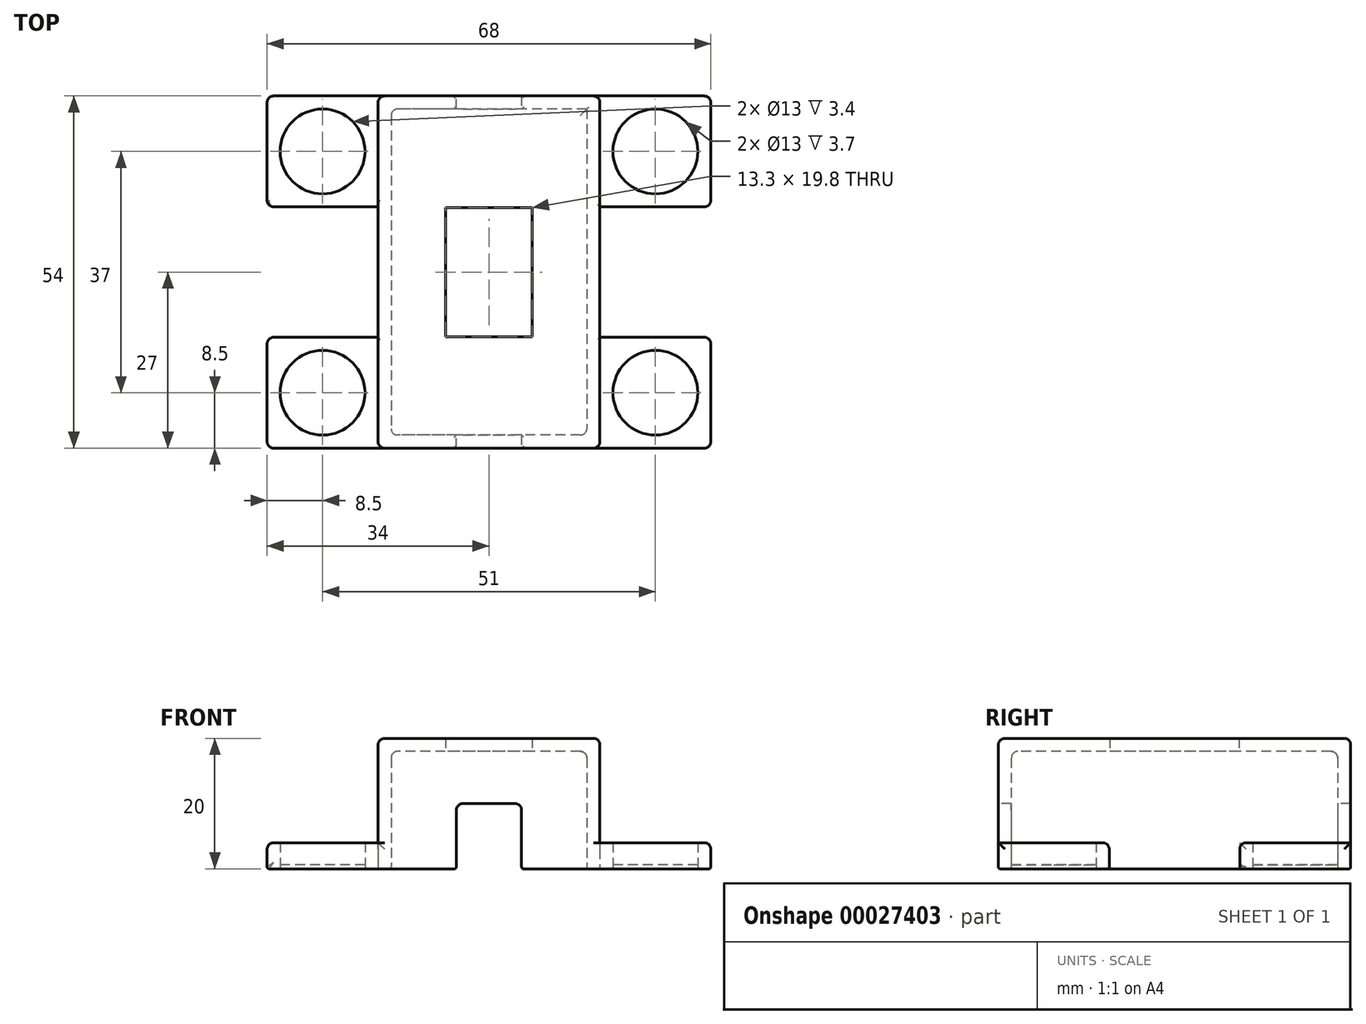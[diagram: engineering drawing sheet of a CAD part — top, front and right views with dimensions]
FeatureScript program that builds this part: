
annotation { "Feature Type Name" : "Feature", "Feature Type Description" : "" }
export const myFeature = defineFeature(function(context is Context, id is Id, definition is map)
    precondition{}
    {
        {
            assignVariable(context, id + "F0", {"name" : "PrintTolerance", "anyValue" : .3});
        }
        {
            assignVariable(context, id + "F1", {"name" : "Height", "anyValue" : 20});
        }
        {
            assignVariable(context, id + "F2", {"name" : "WallThickness", "anyValue" : 2});
        }
        {
            var Q0;
            Q0=qCreatedBy(makeId("Top.planeOp"),FACE);
            var sketch = newSketch(context, id + "F3", { "sketchPlane" : qUnion([Q0])});
            skLineSegment(sketch, "E0.rect.bottom", {"start": v(17, 27) * mm, "end": v(-17, 27) * mm});
            skLineSegment(sketch, "E0.rect.top", {"start": v(17, -27) * mm, "end": v(-17, -27) * mm});
            skLineSegment(sketch, "E0.rect.left", {"start": v(17, 27) * mm, "end": v(17, -27) * mm});
            skLineSegment(sketch, "E0.rect.right", {"start": v(-17, 27) * mm, "end": v(-17, -27) * mm});
            skPoint(sketch, "E0.rect.middle", {"position": v(0, 0) * mm});
            skLineSegment(sketch, "E1", {"start": v(0, -27) * mm, "end": v(0, 27) * mm, "construction": true});
            skLineSegment(sketch, "E2.0", {"start": v(-15, 25) * mm, "end": v(-15, -25) * mm});
            skLineSegment(sketch, "E2.1", {"start": v(15, 25) * mm, "end": v(-15, 25) * mm});
            skLineSegment(sketch, "E2.2", {"start": v(15, 25) * mm, "end": v(15, -25) * mm});
            skLineSegment(sketch, "E2.3", {"start": v(15, -25) * mm, "end": v(-15, -25) * mm});
            skCircle(sketch, "E3", {"center": v(-25.5, 18.5) * mm, "radius": 6.5 * mm});
            skLineSegment(sketch, "E4", {"start": v(-17, 27) * mm, "end": v(-34, 27) * mm});
            skLineSegment(sketch, "E5", {"start": v(-34, 27) * mm, "end": v(-34, 10) * mm});
            skLineSegment(sketch, "E6", {"start": v(-34, 10) * mm, "end": v(-17, 10) * mm});
            skLineSegment(sketch, "E7.MirrorCS", {"start": v(34, 10) * mm, "end": v(17, 10) * mm});
            skCircle(sketch, "E8.MirrorC", {"center": v(25.5, 18.5) * mm, "radius": 6.5 * mm});
            skLineSegment(sketch, "E9.MirrorCS", {"start": v(34, 27) * mm, "end": v(34, 10) * mm});
            skLineSegment(sketch, "E10.MirrorCS", {"start": v(17, 27) * mm, "end": v(34, 27) * mm});
            skLineSegment(sketch, "E11", {"start": v(-17, 0) * mm, "end": v(17, 0) * mm, "construction": true});
            skCircle(sketch, "E12.MirrorC", {"center": v(25.5, -18.5) * mm, "radius": 6.5 * mm});
            skLineSegment(sketch, "E13.MirrorCS", {"start": v(34, -27) * mm, "end": v(34, -10) * mm});
            skLineSegment(sketch, "E14.MirrorCS", {"start": v(17, -27) * mm, "end": v(34, -27) * mm});
            skLineSegment(sketch, "E15.MirrorCS", {"start": v(34, -10) * mm, "end": v(17, -10) * mm});
            skLineSegment(sketch, "E16.MirrorCS", {"start": v(-34, -10) * mm, "end": v(-17, -10) * mm});
            skLineSegment(sketch, "E17.MirrorCS", {"start": v(-34, -27) * mm, "end": v(-34, -10) * mm});
            skLineSegment(sketch, "E18.MirrorCS", {"start": v(-17, -27) * mm, "end": v(-34, -27) * mm});
            skCircle(sketch, "E19.MirrorC", {"center": v(-25.5, -18.5) * mm, "radius": 6.5 * mm});
            skLineSegment(sketch, "E20.bottom", {"start": v(6.65, 9.9) * mm, "end": v(-6.65, 9.9) * mm});
            skLineSegment(sketch, "E20.top", {"start": v(6.65, -9.9) * mm, "end": v(-6.65, -9.9) * mm});
            skLineSegment(sketch, "E20.left", {"start": v(6.65, 9.9) * mm, "end": v(6.65, -9.9) * mm});
            skLineSegment(sketch, "E20.right", {"start": v(-6.65, 9.9) * mm, "end": v(-6.65, -9.9) * mm});
            skSolve(sketch);
        }
        {
            var Q0;
            {var subQ4=sQuery(id+"F3.wireOp",EDGE,"E0.rect.bottom");Q0=makeQuery(id+"F3.imprint","IMPRINT",FACE,{"disambiguationData":[TD([[makeQuery(id+"F3.imprint","IMPRINT",EDGE,{"derivedFrom":subQ4}),1.0]])]});}
            var Q1;
            Q1=makeQuery(id+"F3.imprint","IMPRINT",FACE,{"disambiguationData":[TD([[makeQuery(id+"F3.imprint","IMPRINT",EDGE,{"derivedFrom":sQuery(id+"F3.wireOp",EDGE,"01951cff-519c-4d8f-8b17-a8ba54bfdcde")}),1.0]])]});
            var Q2;
            Q2=makeQuery(id+"F3.imprint","IMPRINT",FACE,{"disambiguationData":[TD([[makeQuery(id+"F3.imprint","IMPRINT",EDGE,{"derivedFrom":sQuery(id+"F3.wireOp",EDGE,"01951cff-519c-4d8f-8b17-a8ba54bfdcde")}),-1.0]])]});
            var Q3;
            Q3=makeQuery(id+"F3.imprint","IMPRINT",FACE,{"disambiguationData":[TD([[makeQuery(id+"F3.imprint","IMPRINT",EDGE,{"derivedFrom":sQuery(id+"F3.wireOp",EDGE,"E2.0")}),1.0]])]});
            extrude(context, id + "F4", {"entities" : qUnion([Q0, Q1, Q2, Q3]), "depth" : (getVariable(context, 'Height')) * mm});
        }
        {
            var Q0;
            Q0=makeQuery(id+"F3.imprint","IMPRINT",FACE,{"disambiguationData":[TD([[makeQuery(id+"F3.imprint","IMPRINT",EDGE,{"derivedFrom":sQuery(id+"F3.wireOp",EDGE,"E2.0")}),1.0]])]});
            extrude(context, id + "F5", {"entities" : qUnion([Q0]), "operationType" : NewBodyOperationType.REMOVE, "depth" : (getVariable(context, 'Height') - getVariable(context, 'WallThickness')) * mm});
        }
        {
            var Q0;
            Q0=makeQuery(id+"F3.imprint","IMPRINT",FACE,{"disambiguationData":[TD([[makeQuery(id+"F3.imprint","IMPRINT",EDGE,{"derivedFrom":sQuery(id+"F3.wireOp",EDGE,"E3")}),-1.0]])]});
            var Q1;
            {var subQ1=sQuery(id+"F3.wireOp",EDGE,"E7.MirrorCS");Q1=makeQuery(id+"F3.imprint","IMPRINT",FACE,{"disambiguationData":[TD([[makeQuery(id+"F3.imprint","IMPRINT",EDGE,{"derivedFrom":subQ1}),-1.0]])]});}
            var Q2;
            Q2=makeQuery(id+"F3.imprint","IMPRINT",FACE,{"disambiguationData":[TD([[makeQuery(id+"F3.imprint","IMPRINT",EDGE,{"derivedFrom":sQuery(id+"F3.wireOp",EDGE,"E12.MirrorC")}),-1.0]])]});
            var Q3;
            {var subQ1=sQuery(id+"F3.wireOp",EDGE,"E16.MirrorCS");Q3=makeQuery(id+"F3.imprint","IMPRINT",FACE,{"disambiguationData":[TD([[makeQuery(id+"F3.imprint","IMPRINT",EDGE,{"derivedFrom":subQ1}),-1.0]])]});}
            extrude(context, id + "F6", {"entities" : qUnion([Q0, Q1, Q2, Q3]), "operationType" : NewBodyOperationType.ADD, "depth" : 4 * mm});
        }
        {
            var Q0;
            Q0=makeQuery(id+"F3.imprint","IMPRINT",FACE,{"disambiguationData":[TD([[makeQuery(id+"F3.imprint","IMPRINT",EDGE,{"derivedFrom":sQuery(id+"F3.wireOp",EDGE,"E8.MirrorC")}),-1.0]])]});
            var Q1;
            Q1=makeQuery(id+"F3.imprint","IMPRINT",FACE,{"disambiguationData":[TD([[makeQuery(id+"F3.imprint","IMPRINT",EDGE,{"derivedFrom":sQuery(id+"F3.wireOp",EDGE,"E12.MirrorC")}),1.0]])]});
            var Q2;
            Q2=makeQuery(id+"F3.imprint","IMPRINT",FACE,{"disambiguationData":[TD([[makeQuery(id+"F3.imprint","IMPRINT",EDGE,{"derivedFrom":sQuery(id+"F3.wireOp",EDGE,"E19.MirrorC")}),-1.0]])]});
            var Q3;
            Q3=makeQuery(id+"F3.imprint","IMPRINT",FACE,{"disambiguationData":[TD([[makeQuery(id+"F3.imprint","IMPRINT",EDGE,{"derivedFrom":sQuery(id+"F3.wireOp",EDGE,"E3")}),1.0]])]});
            extrude(context, id + "F7", {"entities" : qUnion([Q0, Q1, Q2, Q3]), "operationType" : NewBodyOperationType.ADD, "depth" : .6 * mm});
        }
        {
            var Q0;
            Q0=makeQuery(id+"F6.boolean.opBoolean","MERGE",FACE,{"derivedFrom":[makeQuery(id+"F4.opExtrude","SWEPT_FACE",FACE,{"disambiguationData":[OSD([sQuery(id+"F3.wireOp",EDGE,"E0.rect.top")])]}),makeQuery(id+"F6.opExtrude","SWEPT_FACE",FACE,{"disambiguationData":[OSD([sQuery(id+"F3.wireOp",EDGE,"E14.MirrorCS")])]}),makeQuery(id+"F6.opExtrude","SWEPT_FACE",FACE,{"disambiguationData":[OSD([sQuery(id+"F3.wireOp",EDGE,"E18.MirrorCS")])]})]});
            var sketch = newSketch(context, id + "F8", { "sketchPlane" : qUnion([Q0])});
            skLineSegment(sketch, "E21", {"start": v(-5, 0) * mm, "end": v(-5, 10) * mm});
            skLineSegment(sketch, "E22", {"start": v(-5, 10) * mm, "end": v(5, 10) * mm});
            skLineSegment(sketch, "E23", {"start": v(5, 10) * mm, "end": v(5, 0) * mm});
            skLineSegment(sketch, "E24", {"start": v(-5, 0) * mm, "end": v(-5, -3) * mm});
            skLineSegment(sketch, "E25", {"start": v(-5, -3) * mm, "end": v(5, -3) * mm});
            skLineSegment(sketch, "E26", {"start": v(5, -3) * mm, "end": v(5, 0) * mm});
            skSolve(sketch);
        }
        {
            var Q0;
            {var subQ0=sQuery(id+"F8.wireOp",EDGE,"E22");Q0=makeQuery(id+"F8.imprint","IMPRINT",FACE,{"disambiguationData":[TD([[makeQuery(id+"F8.imprint","IMPRINT",EDGE,{"derivedFrom":subQ0}),-1.0]])]});}
            var Q1;
            {var subQ0=sQuery(id+"F8.wireOp",EDGE,"E24");Q1=makeQuery(id+"F8.imprint","IMPRINT",FACE,{"disambiguationData":[TD([[makeQuery(id+"F8.imprint","IMPRINT",EDGE,{"derivedFrom":subQ0}),1.0]])]});}
            extrude(context, id + "F9", {"entities" : qUnion([Q0, Q1]), "operationType" : NewBodyOperationType.REMOVE, "endBound" : BoundingType.THROUGH_ALL, "oppositeDirection" : true, "depth" : 25 * mm});
        }
        {
            var Q0;
            Q0=makeQuery(id+"F6.opExtrude","SWEPT_EDGE",EDGE,{"disambiguationData":[OSD([sQuery(id+"F3.wireOp",EDGE,"E17.MirrorCS"),sQuery(id+"F3.wireOp",EDGE,"E18.MirrorCS")])]});
            var Q1;
            Q1=makeQuery(id+"F6.opExtrude","SWEPT_EDGE",EDGE,{"disambiguationData":[OSD([sQuery(id+"F3.wireOp",EDGE,"E16.MirrorCS"),sQuery(id+"F3.wireOp",EDGE,"E17.MirrorCS")])]});
            var Q2;
            {var subQ0=sQuery(id+"F3.wireOp",EDGE,"E0.rect.right");Q2=makeQuery(id+"F6.opExtrude","CAP_EDGE",EDGE,{"disambiguationData":[OSD([subQ0]),TDD([makeQuery(id+"F3.imprint","IMPRINT",EDGE,{"disambiguationData":[TD([[makeQuery(id+"F3.imprint","INTERSECT",VERTEX,{"derivedFrom":[subQ0,sQuery(id+"F3.wireOp",EDGE,"E16.MirrorCS")]}),-1.0]])],"derivedFrom":subQ0})])],"isStart":false});}
            var Q3;
            Q3=makeQuery(id+"F6.opExtrude","SWEPT_EDGE",EDGE,{"disambiguationData":[OSD([sQuery(id+"F3.wireOp",EDGE,"E0.rect.right"),sQuery(id+"F3.wireOp",EDGE,"E16.MirrorCS")])]});
            var Q4;
            Q4=makeQuery(id+"F6.opExtrude","SWEPT_EDGE",EDGE,{"disambiguationData":[OSD([sQuery(id+"F3.wireOp",EDGE,"E0.rect.right"),sQuery(id+"F3.wireOp",EDGE,"E6")])]});
            var Q5;
            Q5=makeQuery(id+"F6.opExtrude","SWEPT_EDGE",EDGE,{"disambiguationData":[OSD([sQuery(id+"F3.wireOp",EDGE,"E5"),sQuery(id+"F3.wireOp",EDGE,"E6")])]});
            var Q6;
            Q6=makeQuery(id+"F6.opExtrude","SWEPT_EDGE",EDGE,{"disambiguationData":[OSD([sQuery(id+"F3.wireOp",EDGE,"E4"),sQuery(id+"F3.wireOp",EDGE,"E5")])]});
            var Q7;
            {var subQ0=sQuery(id+"F3.wireOp",EDGE,"E0.rect.right");Q7=makeQuery(id+"F6.opExtrude","CAP_EDGE",EDGE,{"disambiguationData":[OSD([subQ0]),TDD([makeQuery(id+"F3.imprint","IMPRINT",EDGE,{"disambiguationData":[TD([[makeQuery(id+"F3.imprint","INTERSECT",VERTEX,{"derivedFrom":[subQ0,sQuery(id+"F3.wireOp",EDGE,"E6")]}),1.0]])],"derivedFrom":subQ0})])],"isStart":false});}
            var Q8;
            Q8=makeQuery(id+"F6.opExtrude","SWEPT_EDGE",EDGE,{"disambiguationData":[OSD([sQuery(id+"F3.wireOp",EDGE,"E0.rect.left"),sQuery(id+"F3.wireOp",EDGE,"E7.MirrorCS")])]});
            var Q9;
            {var subQ0=sQuery(id+"F3.wireOp",EDGE,"E0.rect.left");Q9=makeQuery(id+"F6.opExtrude","CAP_EDGE",EDGE,{"disambiguationData":[OSD([subQ0]),TDD([makeQuery(id+"F3.imprint","IMPRINT",EDGE,{"disambiguationData":[TD([[makeQuery(id+"F3.imprint","INTERSECT",VERTEX,{"derivedFrom":[subQ0,sQuery(id+"F3.wireOp",EDGE,"E7.MirrorCS")]}),1.0]])],"derivedFrom":subQ0})])],"isStart":false});}
            var Q10;
            Q10=makeQuery(id+"F6.opExtrude","SWEPT_EDGE",EDGE,{"disambiguationData":[OSD([sQuery(id+"F3.wireOp",EDGE,"E7.MirrorCS"),sQuery(id+"F3.wireOp",EDGE,"E9.MirrorCS")])]});
            var Q11;
            Q11=makeQuery(id+"F6.opExtrude","SWEPT_EDGE",EDGE,{"disambiguationData":[OSD([sQuery(id+"F3.wireOp",EDGE,"E9.MirrorCS"),sQuery(id+"F3.wireOp",EDGE,"E10.MirrorCS")])]});
            var Q12;
            Q12=makeQuery(id+"F6.opExtrude","SWEPT_EDGE",EDGE,{"disambiguationData":[OSD([sQuery(id+"F3.wireOp",EDGE,"E13.MirrorCS"),sQuery(id+"F3.wireOp",EDGE,"E15.MirrorCS")])]});
            var Q13;
            {var subQ0=sQuery(id+"F3.wireOp",EDGE,"E0.rect.left");Q13=makeQuery(id+"F6.opExtrude","CAP_EDGE",EDGE,{"disambiguationData":[OSD([subQ0]),TDD([makeQuery(id+"F3.imprint","IMPRINT",EDGE,{"disambiguationData":[TD([[makeQuery(id+"F3.imprint","INTERSECT",VERTEX,{"derivedFrom":[subQ0,sQuery(id+"F3.wireOp",EDGE,"E15.MirrorCS")]}),-1.0]])],"derivedFrom":subQ0})])],"isStart":false});}
            var Q14;
            Q14=makeQuery(id+"F6.opExtrude","SWEPT_EDGE",EDGE,{"disambiguationData":[OSD([sQuery(id+"F3.wireOp",EDGE,"E13.MirrorCS"),sQuery(id+"F3.wireOp",EDGE,"E14.MirrorCS")])]});
            var Q15;
            Q15=makeQuery(id+"F6.opExtrude","SWEPT_EDGE",EDGE,{"disambiguationData":[OSD([sQuery(id+"F3.wireOp",EDGE,"E0.rect.left"),sQuery(id+"F3.wireOp",EDGE,"E15.MirrorCS")])]});
            var Q16;
            Q16=makeQuery(id+"F4.opExtrude","SWEPT_EDGE",EDGE,{"disambiguationData":[OSD([sQuery(id+"F3.wireOp",EDGE,"E0.rect.bottom"),sQuery(id+"F3.wireOp",EDGE,"E0.rect.left"),sQuery(id+"F3.wireOp",EDGE,"E10.MirrorCS")])]});
            var Q17;
            Q17=makeQuery(id+"F6.opExtrude","CAP_EDGE",EDGE,{"disambiguationData":[OSD([sQuery(id+"F3.wireOp",EDGE,"E9.MirrorCS")])],"isStart":false});
            var Q18;
            Q18=makeQuery(id+"F6.opExtrude","CAP_EDGE",EDGE,{"disambiguationData":[OSD([sQuery(id+"F3.wireOp",EDGE,"E7.MirrorCS")])],"isStart":false});
            var Q19;
            Q19=makeQuery(id+"F4.opExtrude","SWEPT_EDGE",EDGE,{"disambiguationData":[OSD([sQuery(id+"F3.wireOp",EDGE,"E0.rect.bottom"),sQuery(id+"F3.wireOp",EDGE,"E0.rect.right"),sQuery(id+"F3.wireOp",EDGE,"E4")])]});
            var Q20;
            Q20=makeQuery(id+"F6.opExtrude","CAP_EDGE",EDGE,{"disambiguationData":[OSD([sQuery(id+"F3.wireOp",EDGE,"E4")])],"isStart":false});
            var Q21;
            Q21=makeQuery(id+"F6.opExtrude","CAP_EDGE",EDGE,{"disambiguationData":[OSD([sQuery(id+"F3.wireOp",EDGE,"E5")])],"isStart":false});
            var Q22;
            Q22=makeQuery(id+"F6.opExtrude","CAP_EDGE",EDGE,{"disambiguationData":[OSD([sQuery(id+"F3.wireOp",EDGE,"E6")])],"isStart":true});
            var Q23;
            Q23=makeQuery(id+"F4.opExtrude","SWEPT_EDGE",EDGE,{"disambiguationData":[OSD([sQuery(id+"F3.wireOp",EDGE,"E0.rect.top"),sQuery(id+"F3.wireOp",EDGE,"E0.rect.right"),sQuery(id+"F3.wireOp",EDGE,"E18.MirrorCS")])]});
            var Q24;
            Q24=makeQuery(id+"F6.opExtrude","CAP_EDGE",EDGE,{"disambiguationData":[OSD([sQuery(id+"F3.wireOp",EDGE,"E17.MirrorCS")])],"isStart":false});
            var Q25;
            Q25=makeQuery(id+"F6.opExtrude","CAP_EDGE",EDGE,{"disambiguationData":[OSD([sQuery(id+"F3.wireOp",EDGE,"E16.MirrorCS")])],"isStart":false});
            var Q26;
            Q26=makeQuery(id+"F4.opExtrude","SWEPT_EDGE",EDGE,{"disambiguationData":[OSD([sQuery(id+"F3.wireOp",EDGE,"E0.rect.top"),sQuery(id+"F3.wireOp",EDGE,"E0.rect.left"),sQuery(id+"F3.wireOp",EDGE,"E14.MirrorCS")])]});
            var Q27;
            Q27=makeQuery(id+"F6.opExtrude","CAP_EDGE",EDGE,{"disambiguationData":[OSD([sQuery(id+"F3.wireOp",EDGE,"E13.MirrorCS")])],"isStart":false});
            var Q28;
            Q28=makeQuery(id+"F6.opExtrude","CAP_EDGE",EDGE,{"disambiguationData":[OSD([sQuery(id+"F3.wireOp",EDGE,"E15.MirrorCS")])],"isStart":false});
            var Q29;
            Q29=makeQuery(id+"F4.opExtrude","CAP_EDGE",EDGE,{"disambiguationData":[OSD([sQuery(id+"F3.wireOp",EDGE,"E0.rect.left")])],"isStart":false});
            var Q30;
            Q30=makeQuery(id+"F4.opExtrude","CAP_EDGE",EDGE,{"disambiguationData":[OSD([sQuery(id+"F3.wireOp",EDGE,"E0.rect.right")])],"isStart":false});
            var Q31;
            Q31=makeQuery(id+"F4.opExtrude","CAP_EDGE",EDGE,{"disambiguationData":[OSD([sQuery(id+"F3.wireOp",EDGE,"E0.rect.bottom")])],"isStart":false});
            var Q32;
            Q32=makeQuery(id+"F4.opExtrude","CAP_EDGE",EDGE,{"disambiguationData":[OSD([sQuery(id+"F3.wireOp",EDGE,"E0.rect.top")])],"isStart":false});
            var Q33;
            Q33=makeQuery(id+"F5.boolean.opBoolean","COPY",EDGE,{"derivedFrom":makeQuery(id+"F5.opExtrude","CAP_EDGE",EDGE,{"disambiguationData":[OSD([sQuery(id+"F3.wireOp",EDGE,"E2.3")])],"isStart":false})});
            var Q34;
            Q34=makeQuery(id+"F5.boolean.opBoolean","COPY",EDGE,{"derivedFrom":makeQuery(id+"F5.opExtrude","CAP_EDGE",EDGE,{"disambiguationData":[OSD([sQuery(id+"F3.wireOp",EDGE,"E2.2")])],"isStart":false})});
            var Q35;
            Q35=makeQuery(id+"F5.boolean.opBoolean","COPY",EDGE,{"derivedFrom":makeQuery(id+"F5.opExtrude","SWEPT_EDGE",EDGE,{"disambiguationData":[OSD([sQuery(id+"F3.wireOp",EDGE,"E2.2"),sQuery(id+"F3.wireOp",EDGE,"E2.3")])]})});
            var Q36;
            Q36=makeQuery(id+"F5.boolean.opBoolean","COPY",EDGE,{"derivedFrom":makeQuery(id+"F5.opExtrude","SWEPT_EDGE",EDGE,{"disambiguationData":[OSD([sQuery(id+"F3.wireOp",EDGE,"E2.0"),sQuery(id+"F3.wireOp",EDGE,"E2.3")])]})});
            var Q37;
            Q37=makeQuery(id+"F5.boolean.opBoolean","COPY",EDGE,{"derivedFrom":makeQuery(id+"F5.opExtrude","CAP_EDGE",EDGE,{"disambiguationData":[OSD([sQuery(id+"F3.wireOp",EDGE,"E2.0")])],"isStart":false})});
            var Q38;
            Q38=makeQuery(id+"F5.boolean.opBoolean","COPY",EDGE,{"derivedFrom":makeQuery(id+"F5.opExtrude","CAP_EDGE",EDGE,{"disambiguationData":[OSD([sQuery(id+"F3.wireOp",EDGE,"E2.1")])],"isStart":false})});
            var Q39;
            Q39=makeQuery(id+"F5.boolean.opBoolean","COPY",EDGE,{"derivedFrom":makeQuery(id+"F5.opExtrude","SWEPT_EDGE",EDGE,{"disambiguationData":[OSD([sQuery(id+"F3.wireOp",EDGE,"E2.0"),sQuery(id+"F3.wireOp",EDGE,"E2.1")])]})});
            var Q40;
            {var subQ0=sQuery(id+"F8.wireOp",EDGE,"E21");var subQ1=sQuery(id+"F8.wireOp",EDGE,"E22");Q40=makeQuery(id+"F9.boolean.opBoolean","COPY",EDGE,{"disambiguationData":[TD([makeQuery(id+"F4.opExtrude","SWEPT_FACE",FACE,{"disambiguationData":[OSD([sQuery(id+"F3.wireOp",EDGE,"E0.rect.top")])]})])],"derivedFrom":makeQuery(id+"F9.opExtrude","SWEPT_EDGE",EDGE,{"disambiguationData":[OSD([subQ0,subQ1])]})});}
            var Q41;
            {var subQ0=sQuery(id+"F8.wireOp",EDGE,"E22");var subQ1=sQuery(id+"F8.wireOp",EDGE,"E23");Q41=makeQuery(id+"F9.boolean.opBoolean","COPY",EDGE,{"disambiguationData":[TD([makeQuery(id+"F4.opExtrude","SWEPT_FACE",FACE,{"disambiguationData":[OSD([sQuery(id+"F3.wireOp",EDGE,"E0.rect.top")])]})])],"derivedFrom":makeQuery(id+"F9.opExtrude","SWEPT_EDGE",EDGE,{"disambiguationData":[OSD([subQ0,subQ1])]})});}
            var Q42;
            {var subQ0=sQuery(id+"F8.wireOp",EDGE,"E22");var subQ1=sQuery(id+"F8.wireOp",EDGE,"E23");Q42=makeQuery(id+"F9.boolean.opBoolean","COPY",EDGE,{"disambiguationData":[TD([makeQuery(id+"F4.opExtrude","SWEPT_FACE",FACE,{"disambiguationData":[OSD([sQuery(id+"F3.wireOp",EDGE,"E0.rect.bottom")])]})])],"derivedFrom":makeQuery(id+"F9.opExtrude","SWEPT_EDGE",EDGE,{"disambiguationData":[OSD([subQ0,subQ1])]})});}
            var Q43;
            {var subQ0=sQuery(id+"F8.wireOp",EDGE,"E21");var subQ1=sQuery(id+"F8.wireOp",EDGE,"E22");Q43=makeQuery(id+"F9.boolean.opBoolean","COPY",EDGE,{"disambiguationData":[TD([makeQuery(id+"F4.opExtrude","SWEPT_FACE",FACE,{"disambiguationData":[OSD([sQuery(id+"F3.wireOp",EDGE,"E0.rect.bottom")])]})])],"derivedFrom":makeQuery(id+"F9.opExtrude","SWEPT_EDGE",EDGE,{"disambiguationData":[OSD([subQ0,subQ1])]})});}
            fillet(context, id + "F10", {"entities" : qUnion([Q0, Q1, Q2, Q3, Q4, Q5, Q6, Q7, Q8, Q9, Q10, Q11, Q12, Q13, Q14, Q15, Q16, Q17, Q18, Q19, Q20, Q21, Q22, Q23, Q24, Q25, Q26, Q27, Q28, Q29, Q30, Q31, Q32, Q33, Q34, Q35, Q36, Q37, Q38, Q39, Q40, Q41, Q42, Q43]), "radius" : 1 * mm, "tangentPropagation" : true, "allowEdgeOverflow" : false});
        }
        {
            var Q0;
            {var subQ0=sQuery(id+"F3.wireOp",EDGE,"E19.MirrorC");var subQ1=sQuery(id+"F3.wireOp",EDGE,"E12.MirrorC");var subQ2=sQuery(id+"F3.wireOp",EDGE,"E8.MirrorC");var subQ3=sQuery(id+"F3.wireOp",EDGE,"E3");var subQ4=sQuery(id+"F3.wireOp",EDGE,"E0.rect.right");var subQ5=sQuery(id+"F3.wireOp",EDGE,"E0.rect.left");Q0=makeQuery(id+"F7.boolean.opBoolean","MERGE",FACE,{"derivedFrom":[makeQuery(id+"F6.boolean.opBoolean","MERGE",FACE,{"derivedFrom":[makeQuery(id+"F4.opExtrude","CAP_FACE",FACE,{"disambiguationData":[OSD([sQuery(id+"F3.wireOp",EDGE,"E0.rect.bottom"),sQuery(id+"F3.wireOp",EDGE,"E0.rect.top"),subQ5,subQ4,sQuery(id+"F3.wireOp",EDGE,"E20.bottom"),sQuery(id+"F3.wireOp",EDGE,"E20.top"),sQuery(id+"F3.wireOp",EDGE,"E20.left"),sQuery(id+"F3.wireOp",EDGE,"E20.right")])],"isStart":true}),makeQuery(id+"F6.opExtrude","CAP_FACE",FACE,{"disambiguationData":[OSD([subQ5,sQuery(id+"F3.wireOp",EDGE,"E7.MirrorCS"),subQ2,sQuery(id+"F3.wireOp",EDGE,"E9.MirrorCS"),sQuery(id+"F3.wireOp",EDGE,"E10.MirrorCS")])],"isStart":true}),makeQuery(id+"F6.opExtrude","CAP_FACE",FACE,{"disambiguationData":[OSD([subQ5,subQ1,sQuery(id+"F3.wireOp",EDGE,"E13.MirrorCS"),sQuery(id+"F3.wireOp",EDGE,"E14.MirrorCS"),sQuery(id+"F3.wireOp",EDGE,"E15.MirrorCS")])],"isStart":true}),makeQuery(id+"F6.opExtrude","CAP_FACE",FACE,{"disambiguationData":[OSD([subQ4,subQ3,sQuery(id+"F3.wireOp",EDGE,"E4"),sQuery(id+"F3.wireOp",EDGE,"E5"),sQuery(id+"F3.wireOp",EDGE,"E6")])],"isStart":true}),makeQuery(id+"F6.opExtrude","CAP_FACE",FACE,{"disambiguationData":[OSD([subQ4,sQuery(id+"F3.wireOp",EDGE,"E16.MirrorCS"),sQuery(id+"F3.wireOp",EDGE,"E17.MirrorCS"),sQuery(id+"F3.wireOp",EDGE,"E18.MirrorCS"),subQ0])],"isStart":true})]}),makeQuery(id+"F7.opExtrude","CAP_FACE",FACE,{"disambiguationData":[OSD([subQ3])],"isStart":true}),makeQuery(id+"F7.opExtrude","CAP_FACE",FACE,{"disambiguationData":[OSD([subQ2])],"isStart":true}),makeQuery(id+"F7.opExtrude","CAP_FACE",FACE,{"disambiguationData":[OSD([subQ1])],"isStart":true}),makeQuery(id+"F7.opExtrude","CAP_FACE",FACE,{"disambiguationData":[OSD([subQ0])],"isStart":true})]});}
            fillet(context, id + "F11", {"entities" : qUnion([Q0]), "radius" : (getVariable(context, 'PrintTolerance')) * mm, "tangentPropagation" : true, "allowEdgeOverflow" : false});
        }
    });
